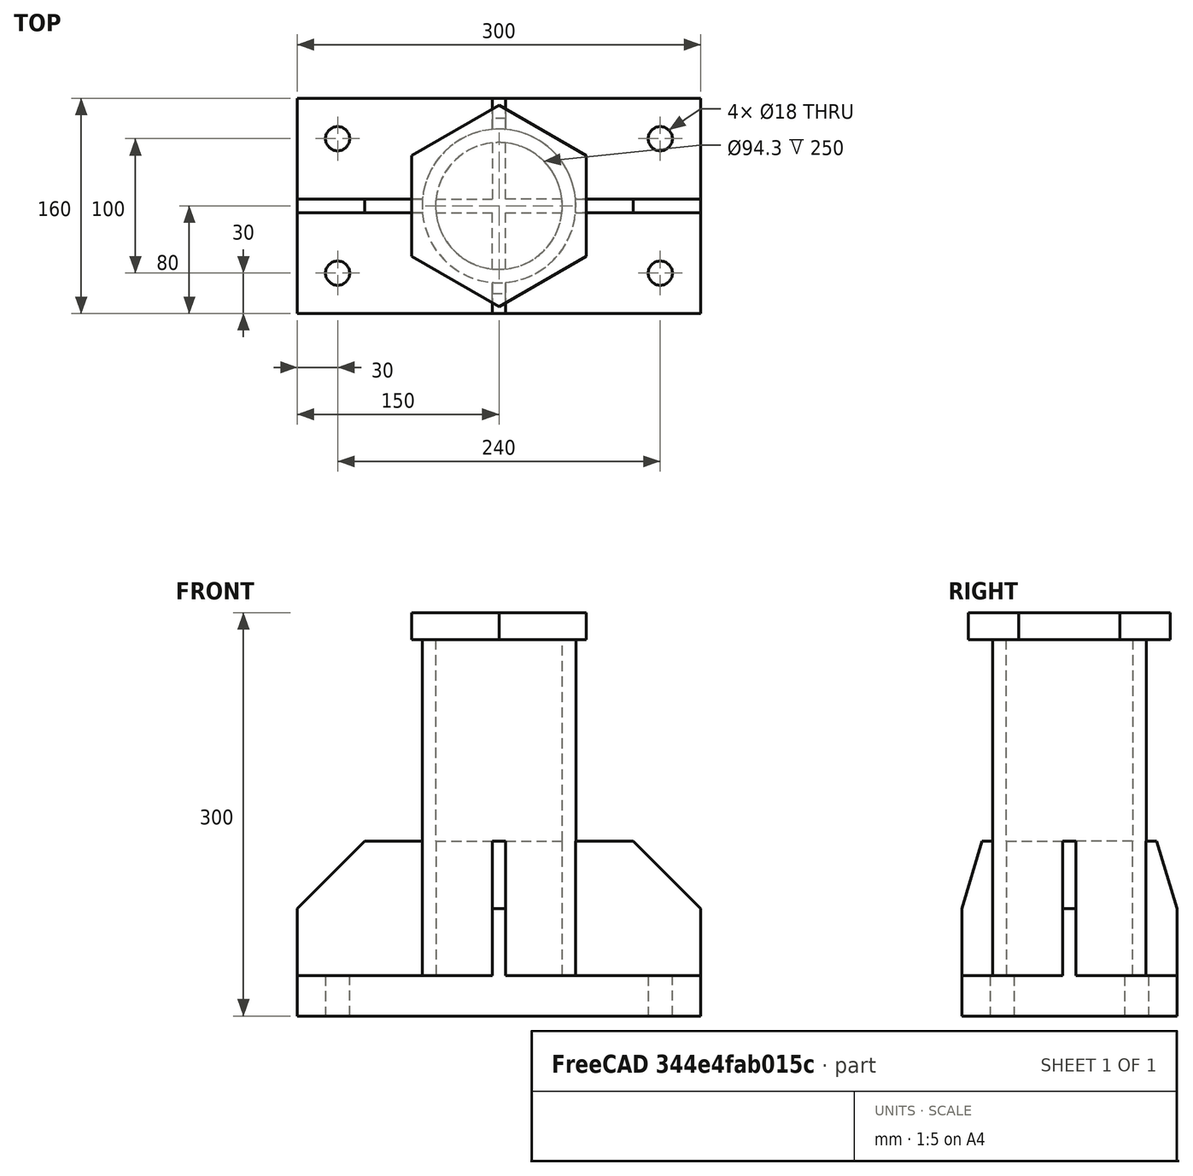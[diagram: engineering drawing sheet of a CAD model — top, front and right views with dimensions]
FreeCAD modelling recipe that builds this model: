
FCSTD DOCUMENT  (FreeCAD 0.21R33694 (Git))
Label: Anschluss_Rahmenfuss_no_fillet
License: All rights reserved
LicenseURL: http://en.wikipedia.org/wiki/All_rights_reserved
objects: Sketcher::SketchObject×5, Part::Extrusion×5, Fem::ConstraintForce×4, Part::MultiFuse×2, Fem::ConstraintFixed×2, Part::FeaturePython×1, Fem::FemSolverObjectPython×1, App::MaterialObjectPython×1, Fem::FeaturePython×1, Fem::FemMeshObjectPython×1, Fem::FemAnalysis×1
note: 13 computed .brp shape members not serialized (recipe doc carries the construction recipe); baked Part::Feature solids carry a one-line shape summary decoded from their .brp

FEATURE [Sketcher::SketchObject] Sketch
  FullyConstrained = true
  sketch-geometry (12):
    g0: LineSegment StartX=-150 StartY=80 StartZ=0 EndX=150 EndY=80 EndZ=0
    g1: LineSegment StartX=150 StartY=80 StartZ=0 EndX=150 EndY=-80 EndZ=0
    g2: LineSegment StartX=150 StartY=-80 StartZ=0 EndX=-150 EndY=-80 EndZ=0
    g3: LineSegment StartX=-150 StartY=-80 StartZ=0 EndX=-150 EndY=80 EndZ=0
    g4: LineSegment StartX=-120 StartY=50 StartZ=0 EndX=120 EndY=50 EndZ=0
    g5: LineSegment StartX=120 StartY=50 StartZ=0 EndX=120 EndY=-50 EndZ=0
    g6: LineSegment StartX=120 StartY=-50 StartZ=0 EndX=-120 EndY=-50 EndZ=0
    g7: LineSegment StartX=-120 StartY=-50 StartZ=0 EndX=-120 EndY=50 EndZ=0
    g8: Circle CenterX=-120 CenterY=50 CenterZ=0 NormalX=0 NormalY=0 NormalZ=1 AngleXU=0 Radius=9
    g9: Circle CenterX=120 CenterY=50 CenterZ=0 NormalX=0 NormalY=0 NormalZ=1 AngleXU=0 Radius=9
    g10: Circle CenterX=120 CenterY=-50 CenterZ=0 NormalX=0 NormalY=0 NormalZ=1 AngleXU=0 Radius=9
    g11: Circle CenterX=-120 CenterY=-50 CenterZ=0 NormalX=0 NormalY=0 NormalZ=1 AngleXU=0 Radius=9
  constraints (28):
    c: Coincident(g0,g1)
    c: Coincident(g1,g2)
    c: Coincident(g2,g3)
    c: Coincident(g3,g0)
    c: Horizontal(g0)
    c: Vertical(g1)
    c: Symmetric(g2,g1,g-2)
    c: Symmetric(g2,g0,g-1)
    c: DistanceX(g2,g2) = 300
    c: DistanceY(g3,g3) = 160
    c: Coincident(g4,g5)
    c: Coincident(g5,g6)
    c: Coincident(g6,g7)
    c: Coincident(g7,g4)
    c: Horizontal(g4)
    c: Vertical(g5)
    c: Symmetric(g6,g5,g-2)
    c: Symmetric(g6,g4,g-1)
    c: DistanceX(g4,g4) = 240
    c: DistanceY(g5,g5) = 100
    c: Coincident(g8,g4)
    c: Coincident(g9,g4)
    c: Coincident(g10,g5)
    c: Coincident(g11,g6)
    c: Equal(g11,g10)
    c: Equal(g11,g9)
    c: Equal(g11,g8)
    c: Diameter(g11) = 18
FEATURE [Part::Extrusion] Extrude  label="platte"
  Base = -> Sketch
  Dir = (0,0,1)
  DirMode = 0
  FaceMakerClass = Part::FaceMakerBullseye
  LengthFwd = 30
  LengthRev = 0
  Solid = true
  Symmetric = false
FEATURE [Sketcher::SketchObject] Sketch001
  ExternalGeometry = -> [Extrude]
  FullyConstrained = true
  Placement = pos=(0,0,0) rot=(1,0,0;1.5708rad)
  sketch-geometry (6):
    g0: LineSegment StartX=150 StartY=30 StartZ=0 EndX=-150 EndY=30 EndZ=0
    g1: LineSegment StartX=-150 StartY=30 StartZ=0 EndX=-150 EndY=80 EndZ=0
    g2: LineSegment StartX=-150 StartY=80 StartZ=0 EndX=-100 EndY=130 EndZ=0
    g3: LineSegment StartX=-100 StartY=130 StartZ=0 EndX=100 EndY=130 EndZ=0
    g4: LineSegment StartX=100 StartY=130 StartZ=0 EndX=150 EndY=80 EndZ=0
    g5: LineSegment StartX=150 StartY=80 StartZ=0 EndX=150 EndY=30 EndZ=0
  constraints (16):
    c: Coincident(g-3,g0)
    c: Horizontal(g0)
    c: Coincident(g0,g1)
    c: Vertical(g1)
    c: Coincident(g1,g2)
    c: Coincident(g2,g3)
    c: Coincident(g3,g4)
    c: Coincident(g4,g5)
    c: Coincident(g5,g0)
    c: Vertical(g5)
    c: Equal(g1,g5)
    c: DistanceX(g0,g0) = 300
    c: Symmetric(g2,g3,g-2)
    c: DistanceX(g3,g3) = 200
    c: DistanceY(g5,g5) = 50
    c: DistanceY(g0,g3) = 100
FEATURE [Part::Extrusion] Extrude001  label="steife1"
  Base = -> Sketch001
  Dir = (0,-1,-3e-16)
  DirMode = 2
  FaceMakerClass = Part::FaceMakerBullseye
  LengthFwd = 10
  LengthRev = 0
  Solid = true
  Symmetric = true
FEATURE [Sketcher::SketchObject] Sketch002
  FullyConstrained = true
  MapMode = 5
  Placement = pos=(0,0,30) rot=(0,0,1;0rad)
  Support = -> [Extrude]
  sketch-geometry (3):
    g0: Circle CenterX=0 CenterY=0 CenterZ=0 NormalX=0 NormalY=0 NormalZ=1 AngleXU=0 Radius=57.15
    g1: Circle CenterX=0 CenterY=0 CenterZ=0 NormalX=0 NormalY=0 NormalZ=1 AngleXU=0 Radius=47.15
    g2: LineSegment StartX=47.15 StartY=0 StartZ=0 EndX=57.15 EndY=0 EndZ=0
  constraints (8):
    c: Coincident(g0,g-1)
    c: Diameter(g0) = 114.3
    c: Coincident(g1,g0)
    c: PointOnObject(g2,g1)
    c: PointOnObject(g2,g0)
    c: PointOnObject(g2,g-1)
    c: Horizontal(g2)
    c: DistanceX(g2,g2) = 10
FEATURE [Part::Extrusion] Extrude002  label="R114x10"
  Base = -> Sketch002
  Dir = (0,0,1)
  DirMode = 0
  FaceMakerClass = Part::FaceMakerBullseye
  LengthFwd = 270
  LengthRev = 0
  Solid = true
  Symmetric = false
FEATURE [Sketcher::SketchObject] Sketch003
  ExternalGeometry = -> [Extrude,Extrude001]
  FullyConstrained = true
  Placement = pos=(0,0,0) rot=(0.57735,0.57735,0.57735;2.0944rad)
  sketch-geometry (5):
    g0: LineSegment StartX=-80 StartY=30 StartZ=0 EndX=-80 EndY=80 EndZ=0
    g1: LineSegment StartX=-5 StartY=130 StartZ=0 EndX=-5 EndY=30 EndZ=0
    g2: LineSegment StartX=-5 StartY=30 StartZ=0 EndX=-80 EndY=30 EndZ=0
    g3: LineSegment StartX=-80 StartY=80 StartZ=0 EndX=-65 EndY=130 EndZ=0
    g4: LineSegment StartX=-65 StartY=130 StartZ=0 EndX=-5 EndY=130 EndZ=0
  constraints (13):
    c: Vertical(g1)
    c: Coincident(g1,g2)
    c: Coincident(g2,g0)
    c: Vertical(g0)
    c: Horizontal(g2)
    c: Coincident(g0,g3)
    c: Coincident(g3,g4)
    c: Coincident(g4,g1)
    c: Horizontal(g4)
    c: Coincident(g1,g-5)
    c: DistanceY(g0,g0) = 50
    c: DistanceX(g0,g3) = 15
    c: Coincident(g-3,g0)
FEATURE [Part::Extrusion] Extrude003  label="steife2"
  Base = -> Sketch003
  Dir = (1,0,0)
  DirMode = 2
  FaceMakerClass = Part::FaceMakerBullseye
  LengthFwd = 10
  LengthRev = 0
  Solid = true
  Symmetric = true
FEATURE [Part::FeaturePython] Clone  label="steife003"  # Draft clone (typed FeaturePython)
  AttacherType = Attacher::AttachEngine3D
  Fuse = false
  Objects = -> [Extrude003]
  Placement = pos=(0,0,0) rot=(0,0,1;3.14159rad)
  Scale = (1,1,1)
FEATURE [Part::MultiFuse] Fusion  label="bauteil"
  Refine = true
  Shapes = -> [Extrude,Extrude001,Extrude002,Extrude003,Clone]
FEATURE [Sketcher::SketchObject] Sketch004
  FullyConstrained = true
  MapMode = 5
  Placement = pos=(0,0,300) rot=(0,0,1;0rad)
  Support = -> [Fusion]
  sketch-geometry (7):
    g0: LineSegment StartX=65 StartY=37.5278 StartZ=0 EndX=0 EndY=75.0555 EndZ=0
    g1: LineSegment StartX=0 StartY=75.0555 StartZ=0 EndX=-65 EndY=37.5278 EndZ=0
    g2: LineSegment StartX=-65 StartY=37.5278 StartZ=0 EndX=-65 EndY=-37.5278 EndZ=0
    g3: LineSegment StartX=-65 StartY=-37.5278 StartZ=0 EndX=0 EndY=-75.0555 EndZ=0
    g4: LineSegment StartX=0 StartY=-75.0555 StartZ=0 EndX=65 EndY=-37.5278 EndZ=0
    g5: LineSegment StartX=65 StartY=-37.5278 StartZ=0 EndX=65 EndY=37.5278 EndZ=0
    g6: Circle CenterX=0 CenterY=0 CenterZ=0 NormalX=0 NormalY=0 NormalZ=1 AngleXU=0 Radius=75.0555
  constraints (16):
    c: Coincident(g0,g1)
    c: Coincident(g1,g2)
    c: Coincident(g2,g3)
    c: Coincident(g3,g4)
    c: Coincident(g4,g5)
    c: Coincident(g5,g0)
    c: Equal(g0, g1-g5) x5
    c: PointOnObject(g0,g6)
    c: PointOnObject(g1,g6)
    c: PointOnObject(g2,g6)
    c: PointOnObject(g3,g6)
    c: PointOnObject(g4,g6)
    c: PointOnObject(g5,g6)
    c: Coincident(g6,g-1)
    c: Vertical(g5)
    c: DistanceX(g1,g0) = 130
FEATURE [Part::Extrusion] Extrude004  label="lastplatte"
  Base = -> Sketch004
  Dir = (0,0,-1)
  DirMode = 0
  FaceMakerClass = Part::FaceMakerBullseye
  LengthFwd = 20
  LengthRev = 0
  Solid = true
  Symmetric = false
FEATURE [Part::MultiFuse] Fusion001
  Refine = true
  Shapes = -> [Fusion,Extrude004]
FEATURE [Fem::FemSolverObjectPython] SolverCcxTools  # FEM object (typed FeaturePython)
  AnalysisType = 0
  BeamShellResultOutput3D = true
  BucklingFactors = 1
  EigenmodeHighLimit = 1000000
  EigenmodeLowLimit = 0
  EigenmodesCount = 10
  GeometricalNonlinearity = 1
  IterationsControlParameterCutb = 0.25,0.5,0.75,0.85,,,1.5,
  IterationsControlParameterIter = 4,8,9,200,10,400,,200,,
  IterationsControlParameterTimeUse = false
  IterationsThermoMechMaximum = 2000
  IterationsUserDefinedIncrementations = false
  IterationsUserDefinedTimeStepLength = false
  MaterialNonlinearity = 1
  MatrixSolverType = 0
  SplitInputWriter = true
  ThermoMechSteadyState = true
  TimeEnd = 1
  TimeInitialStep = 0.01
FEATURE [App::MaterialObjectPython] MaterialSolid  label="S355"  # material (typed FeaturePython)
  Category = 0
  Material = AuthorAndLicense=(c) 2013 Juergen Riegel (CC-BY 3.0),CardName=CalculiX-Steel,Density=7900 kg/m^3,+8 more (map truncated)
FEATURE [Fem::ConstraintFixed] ConstraintFixed
  NormalDirection = (1,-1e-16,0)
  Normals = (32) [(-1,0,0),(0.5,-0.866025,0),(0.5,0.866025,0),(-1,2.44929e-16,0),(-1,0,0),(0.5,-0.866025,0),(0.5,0.866025,0),(-1,2.44929e-16,0),(-1,0,0),+23 more]
  Points = (32) [(-111,-50,30),(-124.5,-42.2058,30),(-124.5,-57.7942,30),(-111,-50,30),(-111,-50,20),(-124.5,-42.2058,20),(-124.5,-57.7942,20),(-111,-50,20),+24 more]
  References = -> [Fusion001]
  Scale = 5
FEATURE [Fem::ConstraintFixed] ConstraintFixed001
  NormalDirection = (1,-1e-16,0)
  Normals = (32) [(-1,0,0),(0.5,-0.866025,0),(0.5,0.866025,0),(-1,2.44929e-16,0),(-1,0,0),(0.5,-0.866025,0),(0.5,0.866025,0),(-1,2.44929e-16,0),(-1,0,0),+23 more]
  Points = (32) [(129,-50,30),(115.5,-42.2058,30),(115.5,-57.7942,30),(129,-50,30),(129,-50,20),(115.5,-42.2058,20),(115.5,-57.7942,20),(129,-50,20),(129,-50,10),+23 more]
  References = -> [Fusion001]
  Scale = 5
FEATURE [Fem::ConstraintForce] ConstraintForce  label="Q"
  Direction = -> Fusion001 [Edge67]
  DirectionVector = (1,0,0)
  Force = 31900
  NormalDirection = (0,0,1)
  Points = (8) [(-65,-25.0185,300),(-21.6667,-25.0185,300),(21.6667,-25.0185,300),(65,-25.0185,300),(-65,25.0185,300),(-21.6667,25.0185,300),(21.6667,25.0185,300),+1 more]
  References = -> [Fusion001]
  Reversed = true
  Scale = 12
FEATURE [Fem::ConstraintForce] ConstraintForce001  label="N"
  DirectionVector = (0,0,1)
  Force = 40500
  NormalDirection = (0,0,1)
  Points = (8) [(-65,-25.0185,300),(-21.6667,-25.0185,300),(21.6667,-25.0185,300),(65,-25.0185,300),(-65,25.0185,300),(-21.6667,25.0185,300),(21.6667,25.0185,300),+1 more]
  References = -> [Fusion001]
  Scale = 12
FEATURE [Fem::ConstraintForce] ConstraintForce002  label="V1"
  Direction = -> Fusion001 [Edge36]
  DirectionVector = (0,0,-1)
  Force = 96000
  NormalDirection = (1,0,0)
  Points = (12) [(65,-37.5278,280),(65,-12.5093,280),(65,12.5093,280),(65,37.5278,280),(65,-37.5278,290),(65,-12.5093,290),(65,12.5093,290),(65,37.5278,290),+4 more]
  References = -> [Fusion001]
  Reversed = true
  Scale = 6
FEATURE [Fem::ConstraintForce] ConstraintForce003  label="V2"
  Direction = -> Fusion001 [Edge70]
  DirectionVector = (0,0,1)
  Force = 96000
  NormalDirection = (-1,-2e-16,0)
  Points = (12) [(-65,37.5278,280),(-65,12.5093,280),(-65,-12.5093,280),(-65,-37.5278,280),(-65,37.5278,290),(-65,12.5093,290),(-65,-12.5093,290),(-65,-37.5278,290),+4 more]
  References = -> [Fusion001]
  Scale = 6
FEATURE [Fem::FeaturePython] MeshRegion  # FEM object (typed FeaturePython)
  CharacteristicLength = 1
  References = -> [Fusion001]
FEATURE [Fem::FemMeshObjectPython] FEMMeshGmsh  # FEM object (typed FeaturePython)
  Algorithm2D = 0
  Algorithm3D = 0
  CharacteristicLengthMax = 5
  CharacteristicLengthMin = 0
  CoherenceMesh = true
  ElementDimension = 0
  ElementOrder = 1
  GeometryTolerance = 1e-06
  GroupsOfNodes = false
  HighOrderOptimize = 0
  MeshRegionList = -> [MeshRegion]
  MeshSizeFromCurvature = 12
  OptimizeNetgen = false
  OptimizeStd = true
  Part = -> Fusion001
  RecombinationAlgorithm = 0
  Recombine3DAll = false
  RecombineAll = false
  SecondOrderLinear = false
FEATURE [Fem::FemAnalysis] Analysis
  Group = -> [SolverCcxTools,MaterialSolid,ConstraintFixed,ConstraintFixed001,ConstraintForce,ConstraintForce001,ConstraintForce002,ConstraintForce003,FEMMeshGmsh]
